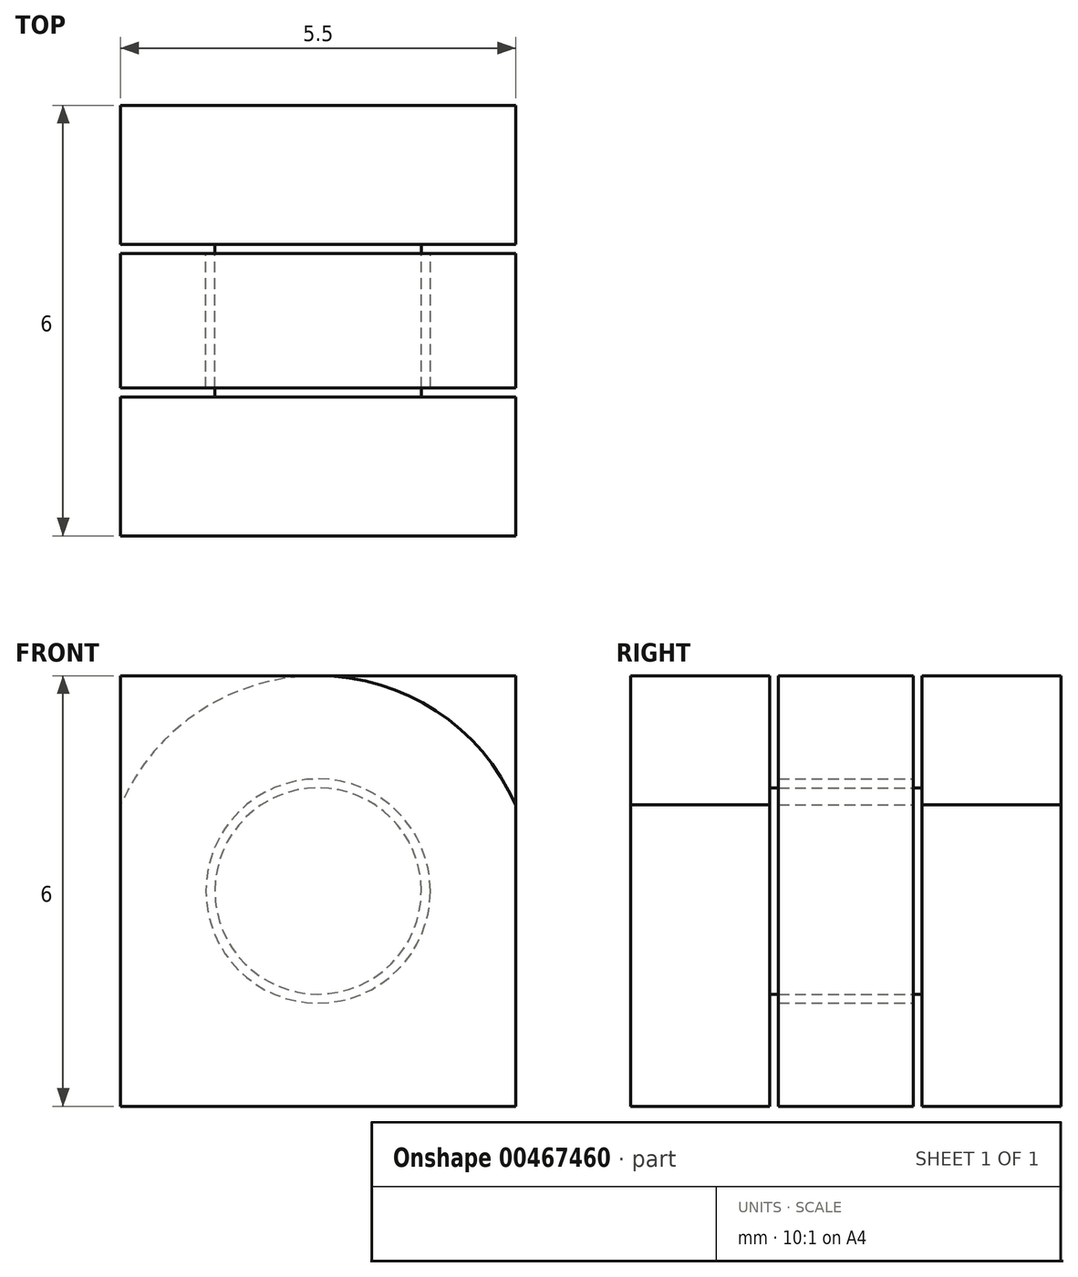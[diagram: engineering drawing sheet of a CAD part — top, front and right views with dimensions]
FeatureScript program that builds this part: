
annotation { "Feature Type Name" : "Feature", "Feature Type Description" : "" }
export const myFeature = defineFeature(function(context is Context, id is Id, definition is map)
    precondition{}
    {
        {
            assignVariable(context, id + "F0", {"name" : "S", "anyValue" : 0.12});
        }
        {
            assignVariable(context, id + "F1", {"name" : "W", "anyValue" : 2});
        }
        {
            var Q0;
            Q0=qCreatedBy(makeId("Front.planeOp"),FACE);
            var sketch = newSketch(context, id + "F2", { "sketchPlane" : qUnion([Q0])});
            skCircle(sketch, "E0", {"center": v(0, 0) * mm, "radius": 1.56 * mm});
            skCircle(sketch, "E1", {"center": v(0, 0) * mm, "radius": 3 * mm});
            skCircle(sketch, "E2", {"center": v(0, 0) * mm, "radius": 1.44 * mm});
            skLineSegment(sketch, "E3", {"start": v(-3, 0) * mm, "end": v(-3, -3) * mm});
            skPoint(sketch, "E4", {"position": v(0, -3) * mm});
            skLineSegment(sketch, "E5", {"start": v(-3, -3) * mm, "end": v(0, -3) * mm});
            skPoint(sketch, "E6", {"position": v(3, 0) * mm});
            skLineSegment(sketch, "E7", {"start": v(0, -3) * mm, "end": v(3, -3) * mm});
            skLineSegment(sketch, "E8", {"start": v(3, -3) * mm, "end": v(3, 0) * mm});
            skLineSegment(sketch, "E9", {"start": v(-3, 0) * mm, "end": v(-3, 3) * mm});
            skLineSegment(sketch, "E10", {"start": v(3, 0) * mm, "end": v(3, 3) * mm});
            skLineSegment(sketch, "E11", {"start": v(-3, 3) * mm, "end": v(0, 3) * mm});
            skLineSegment(sketch, "E12", {"start": v(0, 3) * mm, "end": v(3, 3) * mm});
            skSolve(sketch);
        }
        {
            var Q0;
            Q0=makeQuery(id+"F2.imprint","IMPRINT",FACE,{"disambiguationData":[TD([[makeQuery(id+"F2.imprint","IMPRINT",EDGE,{"derivedFrom":sQuery(id+"F2.wireOp",EDGE,"E2")}),1.0]])]});
            var Q1;
            Q1=makeQuery(id+"F2.imprint","IMPRINT",FACE,{"disambiguationData":[TD([[makeQuery(id+"F2.imprint","IMPRINT",EDGE,{"derivedFrom":sQuery(id+"F2.wireOp",EDGE,"E0")}),1.0]])]});
            var Q2;
            Q2=makeQuery(id+"F2.imprint","IMPRINT",FACE,{"disambiguationData":[TD([[makeQuery(id+"F2.imprint","IMPRINT",EDGE,{"derivedFrom":sQuery(id+"F2.wireOp",EDGE,"E0")}),-1.0]])]});
            var Q3;
            {var subQ0=sQuery(id+"F2.wireOp",EDGE,"E7");Q3=makeQuery(id+"F2.imprint","IMPRINT",FACE,{"disambiguationData":[TD([[makeQuery(id+"F2.imprint","IMPRINT",EDGE,{"derivedFrom":subQ0}),1.0]])]});}
            var Q4;
            {var subQ0=sQuery(id+"F2.wireOp",EDGE,"E3");Q4=makeQuery(id+"F2.imprint","IMPRINT",FACE,{"disambiguationData":[TD([[makeQuery(id+"F2.imprint","IMPRINT",EDGE,{"derivedFrom":subQ0}),1.0]])]});}
            var Q5;
            {var subQ0=sQuery(id+"F2.wireOp",EDGE,"E9");Q5=makeQuery(id+"F2.imprint","IMPRINT",FACE,{"disambiguationData":[TD([[makeQuery(id+"F2.imprint","IMPRINT",EDGE,{"derivedFrom":subQ0}),-1.0]])]});}
            extrude(context, id + "F3", {"entities" : qUnion([Q0, Q1, Q2, Q3, Q4, Q5]), "depth" : 3 * getVariable(context, 'W') * mm, "symmetric" : true});
        }
        {
            var Q0;
            Q0=makeQuery(id+"F2.imprint","IMPRINT",FACE,{"disambiguationData":[TD([[makeQuery(id+"F2.imprint","IMPRINT",EDGE,{"derivedFrom":sQuery(id+"F2.wireOp",EDGE,"E0")}),1.0]])]});
            var Q1;
            Q1=makeQuery(id+"F2.imprint","IMPRINT",FACE,{"disambiguationData":[TD([[makeQuery(id+"F2.imprint","IMPRINT",EDGE,{"derivedFrom":sQuery(id+"F2.wireOp",EDGE,"E0")}),-1.0]])]});
            var Q2;
            {var subQ0=sQuery(id+"F2.wireOp",EDGE,"E7");Q2=makeQuery(id+"F2.imprint","IMPRINT",FACE,{"disambiguationData":[TD([[makeQuery(id+"F2.imprint","IMPRINT",EDGE,{"derivedFrom":subQ0}),1.0]])]});}
            var Q3;
            {var subQ0=sQuery(id+"F2.wireOp",EDGE,"E3");Q3=makeQuery(id+"F2.imprint","IMPRINT",FACE,{"disambiguationData":[TD([[makeQuery(id+"F2.imprint","IMPRINT",EDGE,{"derivedFrom":subQ0}),1.0]])]});}
            var Q4;
            {var subQ0=sQuery(id+"F2.wireOp",EDGE,"E9");Q4=makeQuery(id+"F2.imprint","IMPRINT",FACE,{"disambiguationData":[TD([[makeQuery(id+"F2.imprint","IMPRINT",EDGE,{"derivedFrom":subQ0}),-1.0]])]});}
            extrude(context, id + "F4", {"entities" : qUnion([Q0, Q1, Q2, Q3, Q4]), "operationType" : NewBodyOperationType.REMOVE, "depth" : (getVariable(context, 'W') + getVariable(context, 'S')) * mm, "symmetric" : true});
        }
        {
            var Q0;
            Q0=makeQuery(id+"F2.imprint","IMPRINT",FACE,{"disambiguationData":[TD([[makeQuery(id+"F2.imprint","IMPRINT",EDGE,{"derivedFrom":sQuery(id+"F2.wireOp",EDGE,"E0")}),-1.0]])]});
            var Q1;
            {var subQ0=sQuery(id+"F2.wireOp",EDGE,"E3");Q1=makeQuery(id+"F2.imprint","IMPRINT",FACE,{"disambiguationData":[TD([[makeQuery(id+"F2.imprint","IMPRINT",EDGE,{"derivedFrom":subQ0}),1.0]])]});}
            var Q2;
            {var subQ0=sQuery(id+"F2.wireOp",EDGE,"E7");Q2=makeQuery(id+"F2.imprint","IMPRINT",FACE,{"disambiguationData":[TD([[makeQuery(id+"F2.imprint","IMPRINT",EDGE,{"derivedFrom":subQ0}),1.0]])]});}
            var Q3;
            {var subQ0=sQuery(id+"F2.wireOp",EDGE,"E10");Q3=makeQuery(id+"F2.imprint","IMPRINT",FACE,{"disambiguationData":[TD([[makeQuery(id+"F2.imprint","IMPRINT",EDGE,{"derivedFrom":subQ0}),1.0]])]});}
            extrude(context, id + "F5", {"entities" : qUnion([Q0, Q1, Q2, Q3]), "depth" : (getVariable(context, 'W') - getVariable(context, 'S')) * mm, "symmetric" : true});
        }
        {
            var Q0;
            Q0=qCreatedBy(makeId("Front.planeOp"),FACE);
            var sketch = newSketch(context, id + "F6", { "sketchPlane" : qUnion([Q0])});
            skLineSegment(sketch, "E13.bottom", {"start": v(-2.75, -3) * mm, "end": v(2.75, -3) * mm});
            skLineSegment(sketch, "E13.top", {"start": v(-2.75, 3) * mm, "end": v(2.75, 3) * mm});
            skLineSegment(sketch, "E13.left", {"start": v(-2.75, -3) * mm, "end": v(-2.75, 3) * mm});
            skLineSegment(sketch, "E13.right", {"start": v(2.75, -3) * mm, "end": v(2.75, 3) * mm});
            skPoint(sketch, "E13.middle", {"position": v(0, 0) * mm});
            skLineSegment(sketch, "E14.bottom", {"start": v(2.75, 3) * mm, "end": v(3, 3) * mm});
            skLineSegment(sketch, "E14.top", {"start": v(2.75, -3) * mm, "end": v(3, -3) * mm});
            skLineSegment(sketch, "E14.left", {"start": v(2.75, 3) * mm, "end": v(2.75, -3) * mm});
            skLineSegment(sketch, "E14.right", {"start": v(3, 3) * mm, "end": v(3, -3) * mm});
            skLineSegment(sketch, "E15.bottom", {"start": v(-2.75, 3) * mm, "end": v(-3, 3) * mm});
            skLineSegment(sketch, "E15.top", {"start": v(-2.75, -3) * mm, "end": v(-3, -3) * mm});
            skLineSegment(sketch, "E15.left", {"start": v(-2.75, 3) * mm, "end": v(-2.75, -3) * mm});
            skLineSegment(sketch, "E15.right", {"start": v(-3, 3) * mm, "end": v(-3, -3) * mm});
            skSolve(sketch);
        }
        {
            var Q0;
            Q0=makeQuery(id+"F6.imprint","IMPRINT",FACE,{"disambiguationData":[TD([[makeQuery(id+"F6.imprint","IMPRINT",EDGE,{"derivedFrom":sQuery(id+"F6.wireOp",EDGE,"E15.bottom")}),1.0]])]});
            extrude(context, id + "F7", {"entities" : qUnion([Q0]), "operationType" : NewBodyOperationType.REMOVE, "depth" : 25 * mm, "symmetric" : true});
        }
        {
            var Q0;
            Q0=makeQuery(id+"F6.imprint","IMPRINT",FACE,{"disambiguationData":[TD([[makeQuery(id+"F6.imprint","IMPRINT",EDGE,{"derivedFrom":sQuery(id+"F6.wireOp",EDGE,"E14.bottom")}),-1.0]])]});
            extrude(context, id + "F8", {"entities" : qUnion([Q0]), "operationType" : NewBodyOperationType.REMOVE, "depth" : getVariable(context, 'W') * 3 * mm, "symmetric" : true});
        }
    });
